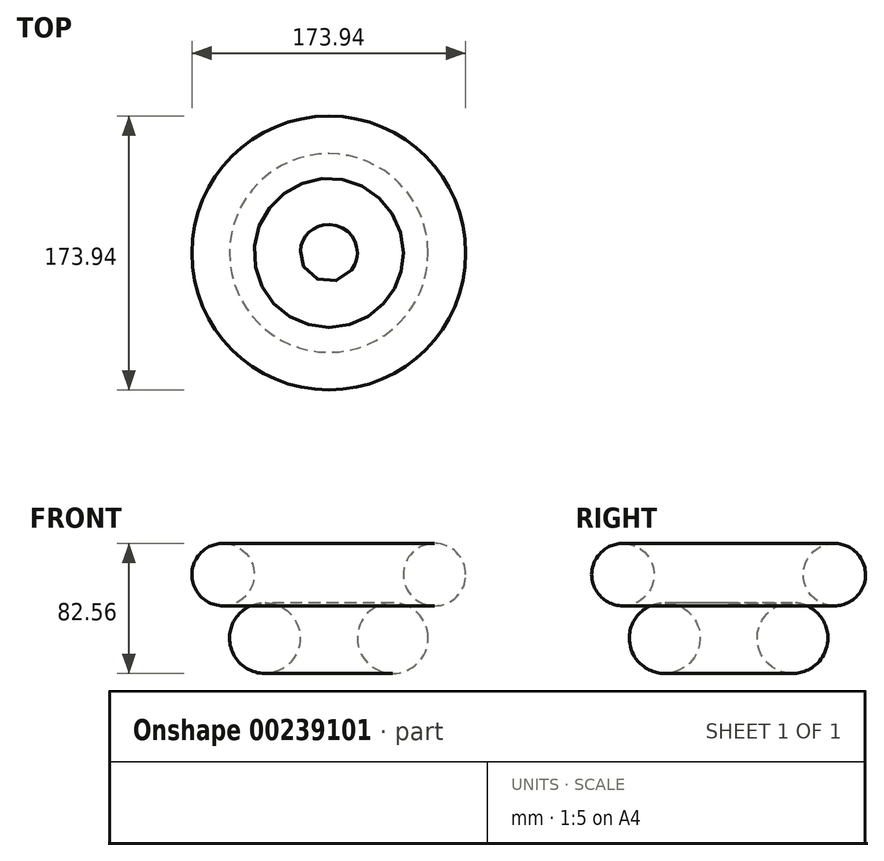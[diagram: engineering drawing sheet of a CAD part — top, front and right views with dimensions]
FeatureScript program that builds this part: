
annotation { "Feature Type Name" : "Feature", "Feature Type Description" : "" }
export const myFeature = defineFeature(function(context is Context, id is Id, definition is map)
    precondition{}
    {
        {
            var Q0;
            Q0=qCreatedBy(makeId("Front.planeOp"),FACE);
            var sketch = newSketch(context, id + "F0", { "sketchPlane" : qUnion([Q0])});
            skCircle(sketch, "E0", {"center": v(40.6, 0) * mm, "radius": 22.45 * mm});
            skLineSegment(sketch, "E1", {"start": v(0, 43.65) * mm, "end": v(0, -30.22) * mm, "construction": true});
            skSolve(sketch);
        }
        {
            var Q0;
            Q0 = qSketchRegion(id + "F0", true);
            var Q1;
            Q1=sQuery(id+"F0.wireOp",EDGE,"E1");
            revolve(context, id + "F1", {"entities" : qUnion([Q0]), "axis" : qUnion([Q1]), "revolveType" : RevolveType.FULL});
        }
        {
            var Q0;
            Q0=qCreatedBy(makeId("Front.planeOp"),FACE);
            var sketch = newSketch(context, id + "F2", { "sketchPlane" : qUnion([Q0])});
            skCircle(sketch, "E2", {"center": v(-67.16, 40.3) * mm, "radius": 19.81 * mm});
            skLineSegment(sketch, "E3", {"start": v(0, 58) * mm, "end": v(0, 23.2) * mm, "construction": true});
            skSolve(sketch);
        }
        {
            var Q0;
            Q0 = qSketchRegion(id + "F2", true);
            var Q1;
            Q1=sQuery(id+"F2.wireOp",EDGE,"E3");
            revolve(context, id + "F3", {"entities" : qUnion([Q0]), "axis" : qUnion([Q1]), "revolveType" : RevolveType.FULL});
        }
    });
